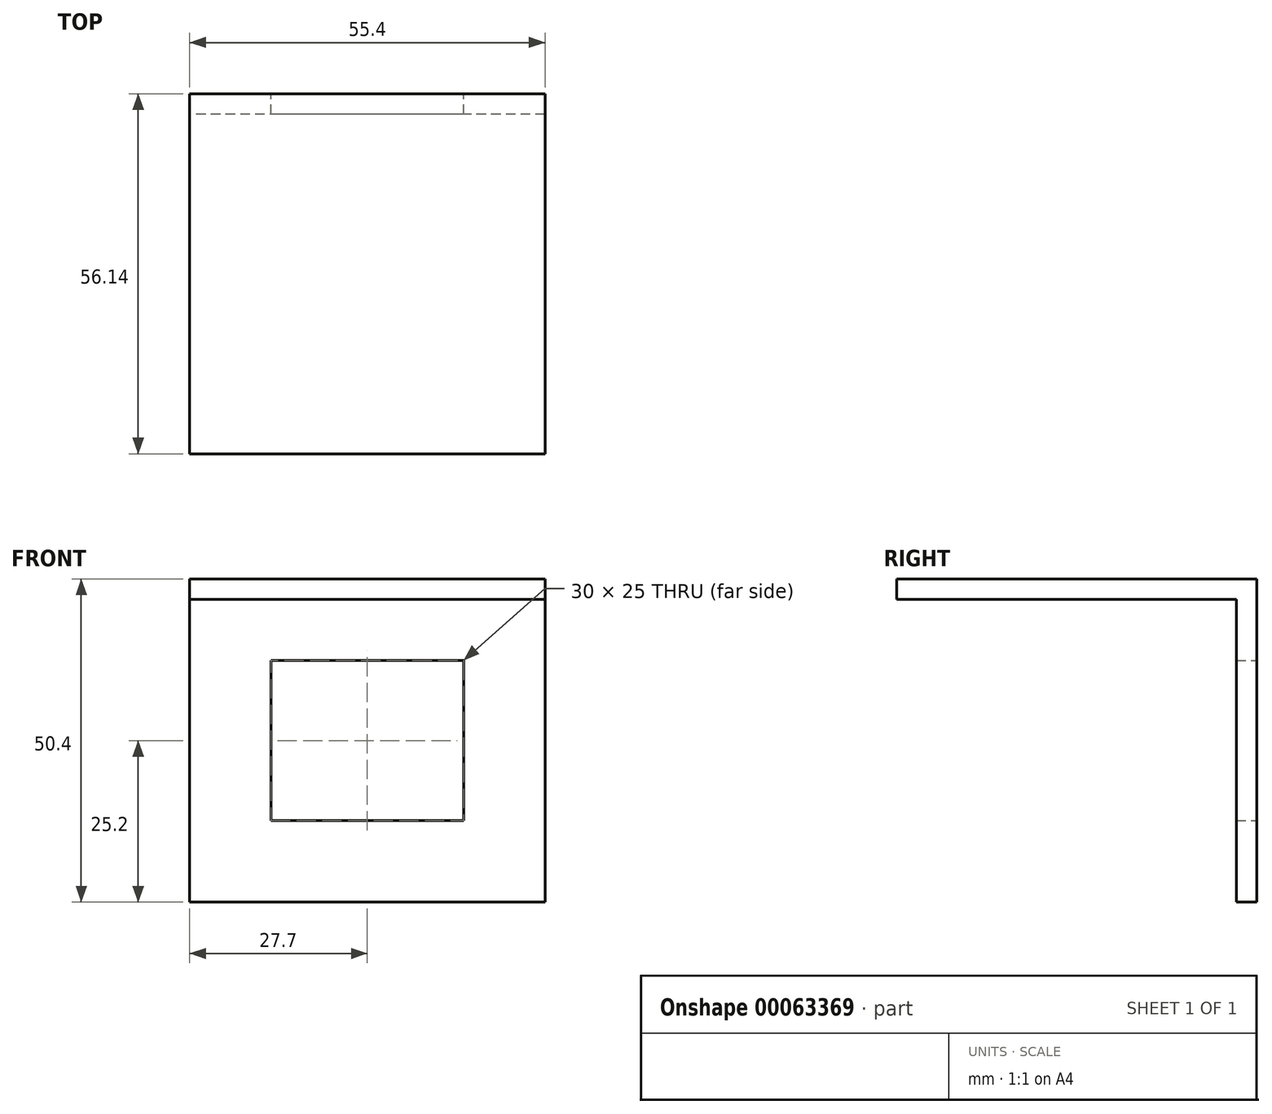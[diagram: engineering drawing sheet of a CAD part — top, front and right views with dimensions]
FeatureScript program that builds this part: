
annotation { "Feature Type Name" : "Feature", "Feature Type Description" : "" }
export const myFeature = defineFeature(function(context is Context, id is Id, definition is map)
    precondition{}
    {
        {
            var Q0;
            Q0=qCreatedBy(makeId("Front.planeOp"),FACE);
            var sketch = newSketch(context, id + "F0", { "sketchPlane" : qUnion([Q0])});
            skLineSegment(sketch, "E0.rect.bottom", {"start": v(15, 12.5) * mm, "end": v(-15, 12.5) * mm});
            skLineSegment(sketch, "E0.rect.top", {"start": v(15, -12.5) * mm, "end": v(-15, -12.5) * mm});
            skLineSegment(sketch, "E0.rect.left", {"start": v(15, 12.5) * mm, "end": v(15, -12.5) * mm});
            skLineSegment(sketch, "E0.rect.right", {"start": v(-15, 12.5) * mm, "end": v(-15, -12.5) * mm});
            skPoint(sketch, "E0.rect.middle", {"position": v(0, 0) * mm});
            skLineSegment(sketch, "E1.0", {"start": v(27.7, 25.2) * mm, "end": v(-27.7, 25.2) * mm});
            skLineSegment(sketch, "E1.1", {"start": v(27.7, 25.2) * mm, "end": v(27.7, -25.2) * mm});
            skLineSegment(sketch, "E1.2", {"start": v(27.7, -25.2) * mm, "end": v(-27.7, -25.2) * mm});
            skLineSegment(sketch, "E1.3", {"start": v(-27.7, 25.2) * mm, "end": v(-27.7, -25.2) * mm});
            skSolve(sketch);
        }
        {
            var Q0;
            Q0=makeQuery(id+"F0.imprint","IMPRINT",FACE,{"disambiguationData":[TD([[makeQuery(id+"F0.imprint","IMPRINT",EDGE,{"derivedFrom":sQuery(id+"F0.wireOp",EDGE,"E0.rect.bottom")}),-1.0]])]});
            extrude(context, id + "F1", {"entities" : qUnion([Q0]), "endBound" : BoundingType.SYMMETRIC, "depth" : 3.17 * mm});
        }
        {
            var Q0;
            Q0=makeQuery(id+"F1.opExtrude","CAP_FACE",FACE,{"disambiguationData":[OSD([sQuery(id+"F0.wireOp",EDGE,"E0.rect.bottom"),sQuery(id+"F0.wireOp",EDGE,"E0.rect.top"),sQuery(id+"F0.wireOp",EDGE,"E0.rect.left"),sQuery(id+"F0.wireOp",EDGE,"E0.rect.right"),sQuery(id+"F0.wireOp",EDGE,"E1.0"),sQuery(id+"F0.wireOp",EDGE,"E1.1"),sQuery(id+"F0.wireOp",EDGE,"E1.2"),sQuery(id+"F0.wireOp",EDGE,"E1.3")])],"isStart":false});
            var sketch = newSketch(context, id + "F2", { "sketchPlane" : qUnion([Q0])});
            skLineSegment(sketch, "E2.bottom", {"start": v(-27.7, 25.2) * mm, "end": v(27.7, 25.2) * mm});
            skLineSegment(sketch, "E2.top", {"start": v(-27.7, 22.03) * mm, "end": v(27.7, 22.03) * mm});
            skLineSegment(sketch, "E2.left", {"start": v(-27.7, 25.2) * mm, "end": v(-27.7, 22.03) * mm});
            skLineSegment(sketch, "E2.right", {"start": v(27.7, 25.2) * mm, "end": v(27.7, 22.03) * mm});
            skSolve(sketch);
        }
        {
            var Q0;
            Q0=makeQuery(id+"F2.imprint","IMPRINT",FACE,{"disambiguationData":[TD([[makeQuery(id+"F2.imprint","IMPRINT",EDGE,{"derivedFrom":sQuery(id+"F2.wireOp",EDGE,"E2.bottom")}),1.0]])]});
            extrude(context, id + "F3", {"entities" : qUnion([Q0]), "operationType" : NewBodyOperationType.ADD, "depth" : 52.96 * mm});
        }
    });
